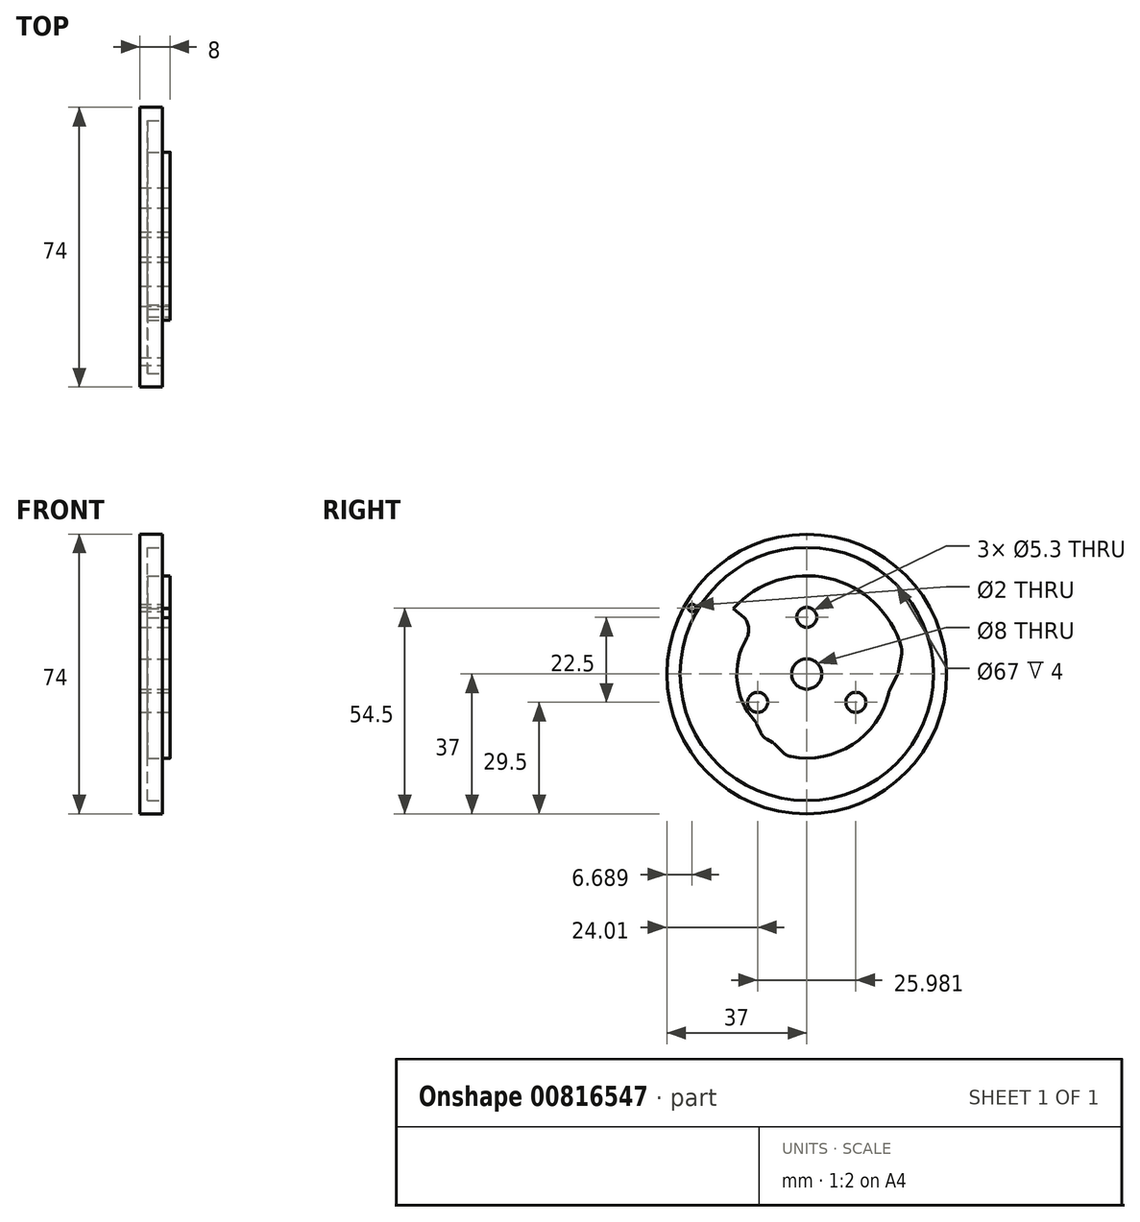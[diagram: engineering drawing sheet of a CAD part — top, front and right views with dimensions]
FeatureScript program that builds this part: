
annotation { "Feature Type Name" : "Feature", "Feature Type Description" : "" }
export const myFeature = defineFeature(function(context is Context, id is Id, definition is map)
    precondition{}
    {
        {
            var Q0;
            Q0=qCreatedBy(makeId("Right.planeOp"),FACE);
            var sketch = newSketch(context, id + "F0", { "sketchPlane" : qUnion([Q0])});
            skCircle(sketch, "E0", {"center": v(0, 0) * mm, "radius": 37 * mm});
            skCircle(sketch, "E1", {"center": v(0, 0) * mm, "radius": 4 * mm});
            skLineSegment(sketch, "E2", {"start": v(0, 50.53) * mm, "end": v(0, -18.5) * mm, "construction": true});
            skLineSegment(sketch, "E3", {"start": v(0, 0) * mm, "end": v(28.08, 48.64) * mm, "construction": true});
            skLineSegment(sketch, "E4", {"start": v(0, 0) * mm, "end": v(48.73, -28.13) * mm, "construction": true});
            skLineSegment(sketch, "E5.MirrorCS", {"start": v(43.76, 25.27) * mm, "end": v(-39.22, -22.65) * mm, "construction": true});
            skLineSegment(sketch, "E6.MirrorCS", {"start": v(0, 0) * mm, "end": v(-28.08, 48.64) * mm, "construction": true});
            skLineSegment(sketch, "E7.MirrorCS", {"start": v(-43.76, 25.27) * mm, "end": v(-19.27, 11.13) * mm, "construction": true});
            skLineSegment(sketch, "E8.MirrorCS", {"start": v(0, 0) * mm, "end": v(-28.08, -48.64) * mm, "construction": true});
            skLineSegment(sketch, "E9.MirrorCS", {"start": v(0, 0) * mm, "end": v(28.08, -48.64) * mm, "construction": true});
            skPoint(sketch, "E10.visualSharp", {"position": v(0, 32) * mm});
            skPoint(sketch, "E11.visualSharp", {"position": v(-14.73, 8.5) * mm});
            skArc(sketch, "E11.filletArc", {"start": v(-14.54, 8.81) * mm, "mid": v(-14.73, 8.5) * mm, "end": v(-14.9, 8.18) * mm});
            skPoint(sketch, "E12.visualSharp", {"position": v(-27.71, -16) * mm});
            skPoint(sketch, "E13.visualSharp", {"position": v(27.71, -16) * mm});
            skCircle(sketch, "E14", {"center": v(0, 0) * mm, "radius": 15 * mm, "construction": true});
            skCircle(sketch, "E15", {"center": v(-13, -7.5) * mm, "radius": 2.65 * mm});
            skCircle(sketch, "E16", {"center": v(13, -7.5) * mm, "radius": 2.65 * mm});
            skCircle(sketch, "E17", {"center": v(0, 15) * mm, "radius": 2.65 * mm});
            skArc(sketch, "E18", {"start": v(-16.02, 9.25) * mm, "mid": v(-18.4, -1.87) * mm, "end": v(-13.83, -12.29) * mm});
            skCircle(sketch, "E19.MirrorC", {"center": v(-30.31, 17.5) * mm, "radius": 1 * mm});
            skArc(sketch, "E20", {"start": v(0, -22.25) * mm, "mid": v(14.01, -17.28) * mm, "end": v(21.77, -4.6) * mm});
            skLineSegment(sketch, "E21", {"start": v(0, -18.5) * mm, "end": v(0, -22.25) * mm});
            skArc(sketch, "E22", {"start": v(-16.02, 9.25) * mm, "mid": v(-15.37, 12.17) * mm, "end": v(-16.5, 14.93) * mm});
            skLineSegment(sketch, "E23.trimOffspring", {"start": v(-16.02, 9.25) * mm, "end": v(19.27, -11.13) * mm, "construction": true});
            skArc(sketch, "E24", {"start": v(-4.2, -21.85) * mm, "mid": v(12.12, -18.66) * mm, "end": v(21.67, -5.06) * mm});
            skLineSegment(sketch, "E25", {"start": v(-12.24, -15.43) * mm, "end": v(-13.16, -13.33) * mm});
            skLineSegment(sketch, "E26", {"start": v(-8.16, -18.83) * mm, "end": v(-6.28, -20.73) * mm});
            skLineSegment(sketch, "E27", {"start": v(-10.58, -17.27) * mm, "end": v(-9, -18.18) * mm});
            skLineSegment(sketch, "E28.trimOffspring", {"start": v(0, -22.25) * mm, "end": v(0, -45.3) * mm, "construction": true});
            skPoint(sketch, "E29.visualSharp", {"position": v(-13.43, -12.73) * mm});
            skArc(sketch, "E29.filletArc", {"start": v(-13.36, -12.88) * mm, "mid": v(-13.44, -12.74) * mm, "end": v(-13.54, -12.6) * mm});
            skArc(sketch, "E30.filletArc", {"start": v(-13.16, -13.33) * mm, "mid": v(-13.46, -12.78) * mm, "end": v(-13.83, -12.29) * mm});
            skPoint(sketch, "E31.visualSharp", {"position": v(-11.7, -16.62) * mm});
            skArc(sketch, "E31.filletArc", {"start": v(-12.24, -15.43) * mm, "mid": v(-11.55, -16.48) * mm, "end": v(-10.58, -17.27) * mm});
            skPoint(sketch, "E32.visualSharp", {"position": v(-8.54, -18.45) * mm});
            skArc(sketch, "E32.filletArc", {"start": v(-8.16, -18.83) * mm, "mid": v(-8.56, -18.48) * mm, "end": v(-9, -18.18) * mm});
            skPoint(sketch, "E33.visualSharp", {"position": v(-5.46, -21.57) * mm});
            skArc(sketch, "E33.filletArc", {"start": v(-6.28, -20.73) * mm, "mid": v(-5.32, -21.45) * mm, "end": v(-4.2, -21.85) * mm});
            skLineSegment(sketch, "E34", {"start": v(-16.5, 14.93) * mm, "end": v(-19.41, 17.3) * mm});
            skArc(sketch, "E35", {"start": v(25, 7.14) * mm, "mid": v(3.18, 25.8) * mm, "end": v(-22.52, 13) * mm});
            skLineSegment(sketch, "E36", {"start": v(22, -4.15) * mm, "end": v(23.85, -0.53) * mm});
            skLineSegment(sketch, "E37", {"start": v(24.23, 0.58) * mm, "end": v(25.1, 5.33) * mm});
            skLineSegment(sketch, "E38.trimOffspring", {"start": v(27.71, -16) * mm, "end": v(39.22, -22.65) * mm, "construction": true});
            skPoint(sketch, "E39.visualSharp", {"position": v(25.25, 6.2) * mm});
            skArc(sketch, "E39.filletArc", {"start": v(25.1, 5.33) * mm, "mid": v(25.15, 6.24) * mm, "end": v(25, 7.14) * mm});
            skPoint(sketch, "E40.visualSharp", {"position": v(24.12, 0) * mm});
            skArc(sketch, "E40.filletArc", {"start": v(23.85, -0.53) * mm, "mid": v(24.08, 0.01) * mm, "end": v(24.23, 0.58) * mm});
            skPoint(sketch, "E41.visualSharp", {"position": v(21.77, -4.6) * mm});
            skArc(sketch, "E41.filletArc", {"start": v(22, -4.15) * mm, "mid": v(21.8, -4.6) * mm, "end": v(21.67, -5.06) * mm});
            skArc(sketch, "E42.0", {"start": v(-6.1, -31.77) * mm, "mid": v(17.62, -27.13) * mm, "end": v(31.5, -7.36) * mm});
            skLineSegment(sketch, "E43.0", {"start": v(31, -8.75) * mm, "end": v(32.84, -5.13) * mm});
            skLineSegment(sketch, "E44.0", {"start": v(34.17, -1.22) * mm, "end": v(35.03, 3.53) * mm});
            skArc(sketch, "E45.0", {"start": v(34.71, 9.91) * mm, "mid": v(4.42, 35.83) * mm, "end": v(-31.26, 18.05) * mm});
            skArc(sketch, "E46.0", {"start": v(-24.77, 14.3) * mm, "mid": v(-28.45, -2.9) * mm, "end": v(-21.38, -19) * mm});
            skLineSegment(sketch, "E47.0", {"start": v(-15.35, -25.93) * mm, "end": v(-13.47, -27.83) * mm});
            skArc(sketch, "E48.0", {"start": v(-13.47, -27.83) * mm, "mid": v(-10.08, -30.36) * mm, "end": v(-6.1, -31.77) * mm});
            skLineSegment(sketch, "E49.0", {"start": v(-21.48, -19.5) * mm, "end": v(-22.4, -17.4) * mm});
            skArc(sketch, "E50.0", {"start": v(-21.48, -19.5) * mm, "mid": v(-19.07, -23.23) * mm, "end": v(-15.63, -26.02) * mm});
            skArc(sketch, "E51.0", {"start": v(32.84, -5.13) * mm, "mid": v(33.65, -3.22) * mm, "end": v(34.17, -1.22) * mm});
            skArc(sketch, "E52.0", {"start": v(35.03, 3.53) * mm, "mid": v(35.24, 6.74) * mm, "end": v(34.71, 9.91) * mm});
            skLineSegment(sketch, "E53", {"start": v(-31.26, 18.05) * mm, "end": v(-24.77, 14.3) * mm});
            skSolve(sketch);
        }
        {
            var Q0;
            Q0 = qSketchRegion(id + "F0", true);
            var Q1;
            Q1=makeQuery(id+"F0.imprint","IMPRINT",FACE,{"disambiguationData":[TD([[makeQuery(id+"F0.imprint","IMPRINT",EDGE,{"derivedFrom":sQuery(id+"F0.wireOp",EDGE,"E1")}),-1.0]])]});
            var Q2;
            Q2=makeQuery(id+"F0.imprint","IMPRINT",FACE,{"disambiguationData":[TD([[makeQuery(id+"F0.imprint","IMPRINT",EDGE,{"derivedFrom":sQuery(id+"F0.wireOp",EDGE,"fmaITuh8-1pOd-9VWb-JPiM-VdxlWLn1jFGd")}),-1.0]])]});
            var Q3;
            Q3=makeQuery(id+"F0.imprint","IMPRINT",FACE,{"disambiguationData":[TD([[makeQuery(id+"F0.imprint","IMPRINT",EDGE,{"derivedFrom":sQuery(id+"F0.wireOp",EDGE,"GR2KLOfM-tpHw-qnjI-VizN-KsQKzkjFn2eF")}),1.0]])]});
            extrude(context, id + "F1", {"entities" : qUnion([Q0, Q1, Q2, Q3]), "oppositeDirection" : true, "depth" : 8 * mm, "offsetDistance" : 25 * mm});
        }
        {
            var Q0;
            Q0=makeQuery(id+"F0.imprint","IMPRINT",FACE,{"disambiguationData":[TD([[makeQuery(id+"F0.imprint","IMPRINT",EDGE,{"derivedFrom":sQuery(id+"F0.wireOp",EDGE,"E0")}),1.0]])]});
            extrude(context, id + "F2", {"entities" : qUnion([Q0]), "operationType" : NewBodyOperationType.REMOVE, "oppositeDirection" : true, "depth" : 2 * mm, "offsetDistance" : 25 * mm});
        }
        {
            var Q0;
            Q0=makeQuery(id+"F2.boolean.opBoolean","COPY",FACE,{"derivedFrom":makeQuery(id+"F2.opExtrude","CAP_FACE",FACE,{"disambiguationData":[OSD([sQuery(id+"F0.wireOp",EDGE,"E0"),sQuery(id+"F0.wireOp",EDGE,"E18")])],"isStart":false})});
            var sketch = newSketch(context, id + "F3", { "sketchPlane" : qUnion([Q0])});
            skCircle(sketch, "E54", {"center": v(0, 0) * mm, "radius": 33.5 * mm});
            skCircle(sketch, "E55", {"center": v(0, 0) * mm, "radius": 18.5 * mm});
            skLineSegment(sketch, "E56", {"start": v(-15.61, -25.62) * mm, "end": v(-13.5, -27.42) * mm});
            skSolve(sketch);
        }
        {
            var Q0;
            Q0=makeQuery(id+"F3.imprint","IMPRINT",FACE,{"disambiguationData":[TD([[makeQuery(id+"F3.imprint","IMPRINT",EDGE,{"derivedFrom":sQuery(id+"F3.wireOp",EDGE,"E54")}),1.0]])]});
            extrude(context, id + "F4", {"entities" : qUnion([Q0]), "operationType" : NewBodyOperationType.REMOVE, "oppositeDirection" : true, "depth" : 4 * mm, "offsetDistance" : 25 * mm});
        }
    });
